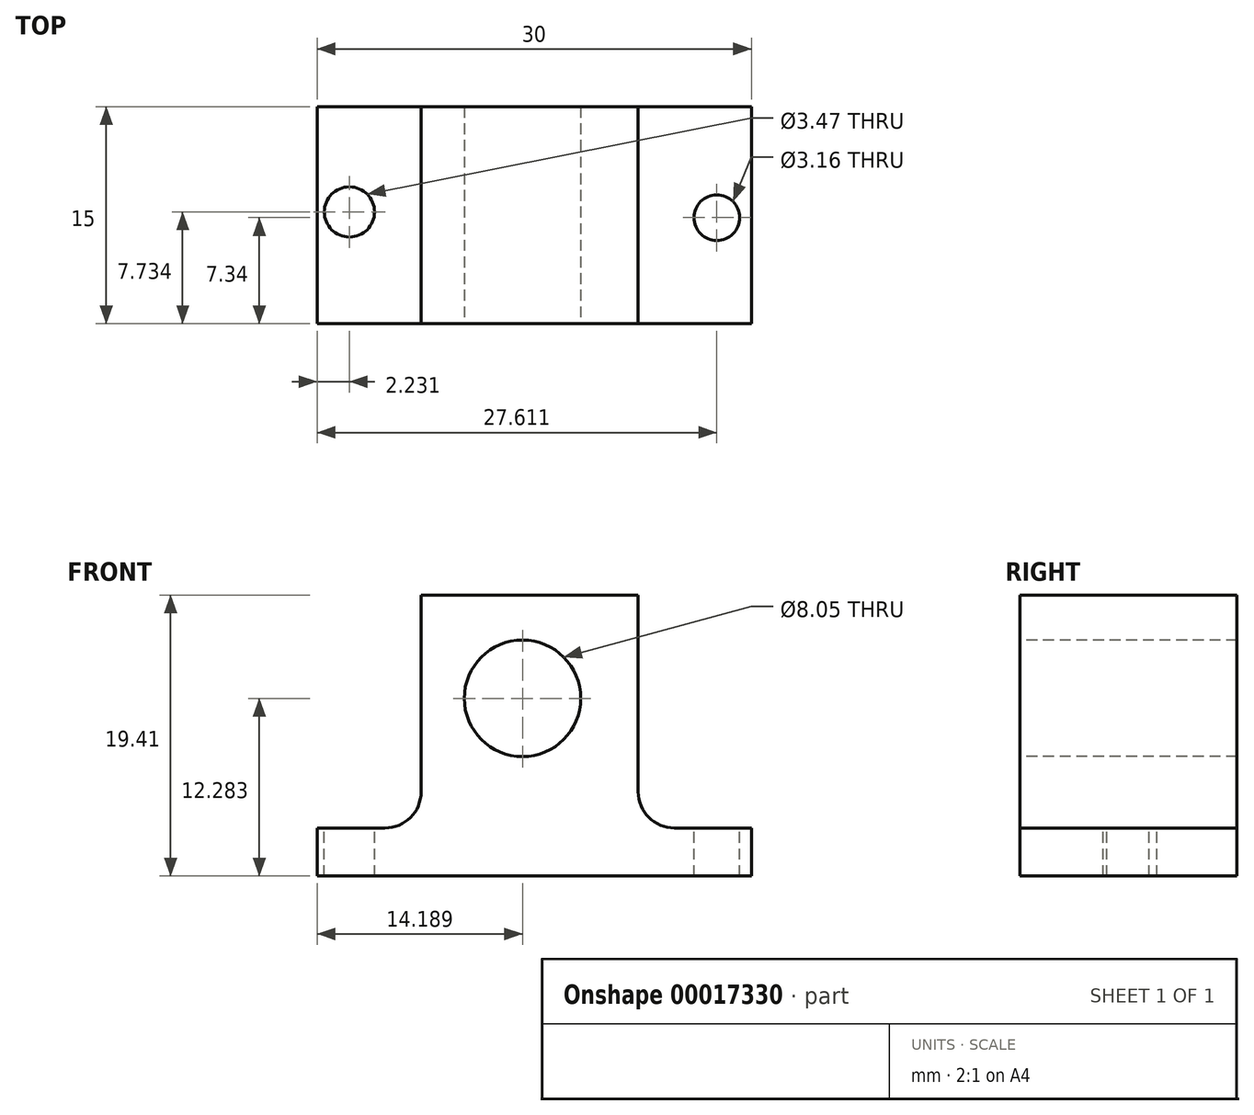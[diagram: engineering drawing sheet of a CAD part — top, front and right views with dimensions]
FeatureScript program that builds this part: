
annotation { "Feature Type Name" : "Feature", "Feature Type Description" : "" }
export const myFeature = defineFeature(function(context is Context, id is Id, definition is map)
    precondition{}
    {
        {
            var Q0;
            Q0=qCreatedBy(makeId("Front.planeOp"),FACE);
            var sketch = newSketch(context, id + "F0", { "sketchPlane" : qUnion([Q0])});
            skLineSegment(sketch, "E0.bottom", {"start": v(-4.77, 19.41) * mm, "end": v(10.23, 19.41) * mm});
            skLineSegment(sketch, "E0.left", {"start": v(-4.77, 19.41) * mm, "end": v(-4.77, 5.82) * mm});
            skLineSegment(sketch, "E0.right", {"start": v(10.23, 19.41) * mm, "end": v(10.23, 5.82) * mm});
            skLineSegment(sketch, "E1.top", {"start": v(-11.95, 0) * mm, "end": v(18.05, 0) * mm});
            skLineSegment(sketch, "E1.left", {"start": v(-11.95, 3.32) * mm, "end": v(-11.95, 0) * mm});
            skLineSegment(sketch, "E1.right", {"start": v(18.05, 3.32) * mm, "end": v(18.05, 0) * mm});
            skLineSegment(sketch, "E2", {"start": v(-11.95, 3.32) * mm, "end": v(-7.27, 3.32) * mm});
            skLineSegment(sketch, "E3", {"start": v(12.73, 3.32) * mm, "end": v(18.05, 3.32) * mm});
            skPoint(sketch, "E4.visualSharp", {"position": v(10.23, 3.32) * mm});
            skArc(sketch, "E4.filletArc", {"start": v(10.23, 5.82) * mm, "mid": v(10.97, 4.05) * mm, "end": v(12.73, 3.32) * mm});
            skPoint(sketch, "E5.visualSharp", {"position": v(-4.77, 3.32) * mm});
            skArc(sketch, "E5.filletArc", {"start": v(-7.27, 3.32) * mm, "mid": v(-5.5, 4.05) * mm, "end": v(-4.77, 5.82) * mm});
            skSolve(sketch);
        }
        {
            var Q0;
            Q0=makeQuery(id+"F0.imprint","IMPRINT",FACE,{"disambiguationData":[TD([[makeQuery(id+"F0.imprint","IMPRINT",EDGE,{"derivedFrom":sQuery(id+"F0.wireOp",EDGE,"E0.bottom")}),-1.0]])]});
            extrude(context, id + "F1", {"entities" : qUnion([Q0]), "depth" : 15 * mm});
        }
        {
            var Q0;
            Q0=makeQuery(id+"F1.opExtrude","CAP_FACE",FACE,{"disambiguationData":[OSD([sQuery(id+"F0.wireOp",EDGE,"E0.bottom"),sQuery(id+"F0.wireOp",EDGE,"E0.left"),sQuery(id+"F0.wireOp",EDGE,"E0.right"),sQuery(id+"F0.wireOp",EDGE,"E1.top"),sQuery(id+"F0.wireOp",EDGE,"E1.left"),sQuery(id+"F0.wireOp",EDGE,"E1.right"),sQuery(id+"F0.wireOp",EDGE,"E2"),sQuery(id+"F0.wireOp",EDGE,"E3"),sQuery(id+"F0.wireOp",EDGE,"E4.filletArc"),sQuery(id+"F0.wireOp",EDGE,"E5.filletArc")])],"isStart":false});
            var sketch = newSketch(context, id + "F2", { "sketchPlane" : qUnion([Q0])});
            skCircle(sketch, "E6", {"center": v(2.24, 12.28) * mm, "radius": 4.02 * mm});
            skSolve(sketch);
        }
        {
            var Q0;
            Q0=makeQuery(id+"F2.imprint","IMPRINT",FACE,{"disambiguationData":[TD([[makeQuery(id+"F2.imprint","IMPRINT",EDGE,{"derivedFrom":sQuery(id+"F2.wireOp",EDGE,"E6")}),1.0]])]});
            extrude(context, id + "F3", {"entities" : qUnion([Q0]), "operationType" : NewBodyOperationType.REMOVE, "oppositeDirection" : true, "depth" : 25 * mm});
        }
        {
            var Q0;
            Q0=makeQuery(id+"F1.opExtrude","SWEPT_FACE",FACE,{"disambiguationData":[OSD([sQuery(id+"F0.wireOp",EDGE,"E2")])]});
            var sketch = newSketch(context, id + "F4", { "sketchPlane" : qUnion([Q0])});
            skCircle(sketch, "E7", {"center": v(-9.72, -7.27) * mm, "radius": 1.73 * mm});
            skCircle(sketch, "E8", {"center": v(15.66, -7.66) * mm, "radius": 1.62 * mm});
            skSolve(sketch);
        }
        {
            var Q0;
            Q0=makeQuery(id+"F1.opExtrude","SWEPT_FACE",FACE,{"disambiguationData":[OSD([sQuery(id+"F0.wireOp",EDGE,"E3")])]});
            var sketch = newSketch(context, id + "F5", { "sketchPlane" : qUnion([Q0])});
            skCircle(sketch, "E9", {"center": v(15.66, -7.66) * mm, "radius": 1.58 * mm});
            skSolve(sketch);
        }
        {
            var Q0;
            Q0=makeQuery(id+"F4.imprint","IMPRINT",FACE,{"disambiguationData":[TD([[makeQuery(id+"F4.imprint","IMPRINT",EDGE,{"derivedFrom":sQuery(id+"F4.wireOp",EDGE,"E7")}),1.0]])]});
            extrude(context, id + "F6", {"entities" : qUnion([Q0]), "operationType" : NewBodyOperationType.REMOVE, "oppositeDirection" : true, "depth" : 25 * mm});
        }
        {
            var Q0;
            Q0=makeQuery(id+"F5.imprint","IMPRINT",FACE,{"disambiguationData":[TD([[makeQuery(id+"F5.imprint","IMPRINT",EDGE,{"derivedFrom":sQuery(id+"F5.wireOp",EDGE,"E9")}),1.0]])]});
            extrude(context, id + "F7", {"entities" : qUnion([Q0]), "operationType" : NewBodyOperationType.REMOVE, "oppositeDirection" : true, "depth" : 25 * mm});
        }
    });
